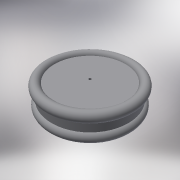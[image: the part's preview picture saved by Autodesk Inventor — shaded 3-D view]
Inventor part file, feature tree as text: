
AUTODESK INVENTOR PART (.ipt)
format: ipt  version: 2016 (Build 200138000, 138)  size: 178,688 bytes
history: native  units: mm
features: sketch x2, revolve x1, extrude x1
ambient origin geometry x8: Origin, YZ Plane, XZ Plane, XY Plane, X Axis, Y Axis, Z Axis, Center Point
bodies: Solid1 (feature_tree)
feature tree (4):
  revolve  "Revolution1"  [1 undecoded]
  extrude  "Extrusion1"  Depth=1.0mm
  sketch  "Sketch1"  dims[d0=15.0mm d1=7.5mm d2=31.5mm]
  sketch  "Sketch2"  dims[d4=1.0mm d5=1.0mm d6=7.0mm d7=7.0mm d8=1.0mm d9=1.0mm d10=15.0mm d11=90.0deg d12=2.0mm d13=10.0mm d14=0.0mm]
note: 1 required parameter value undecoded (feature->parameter linkage not recoverable at this tier; creation-order binding heuristic only, values carry confidence <= 0.55)
